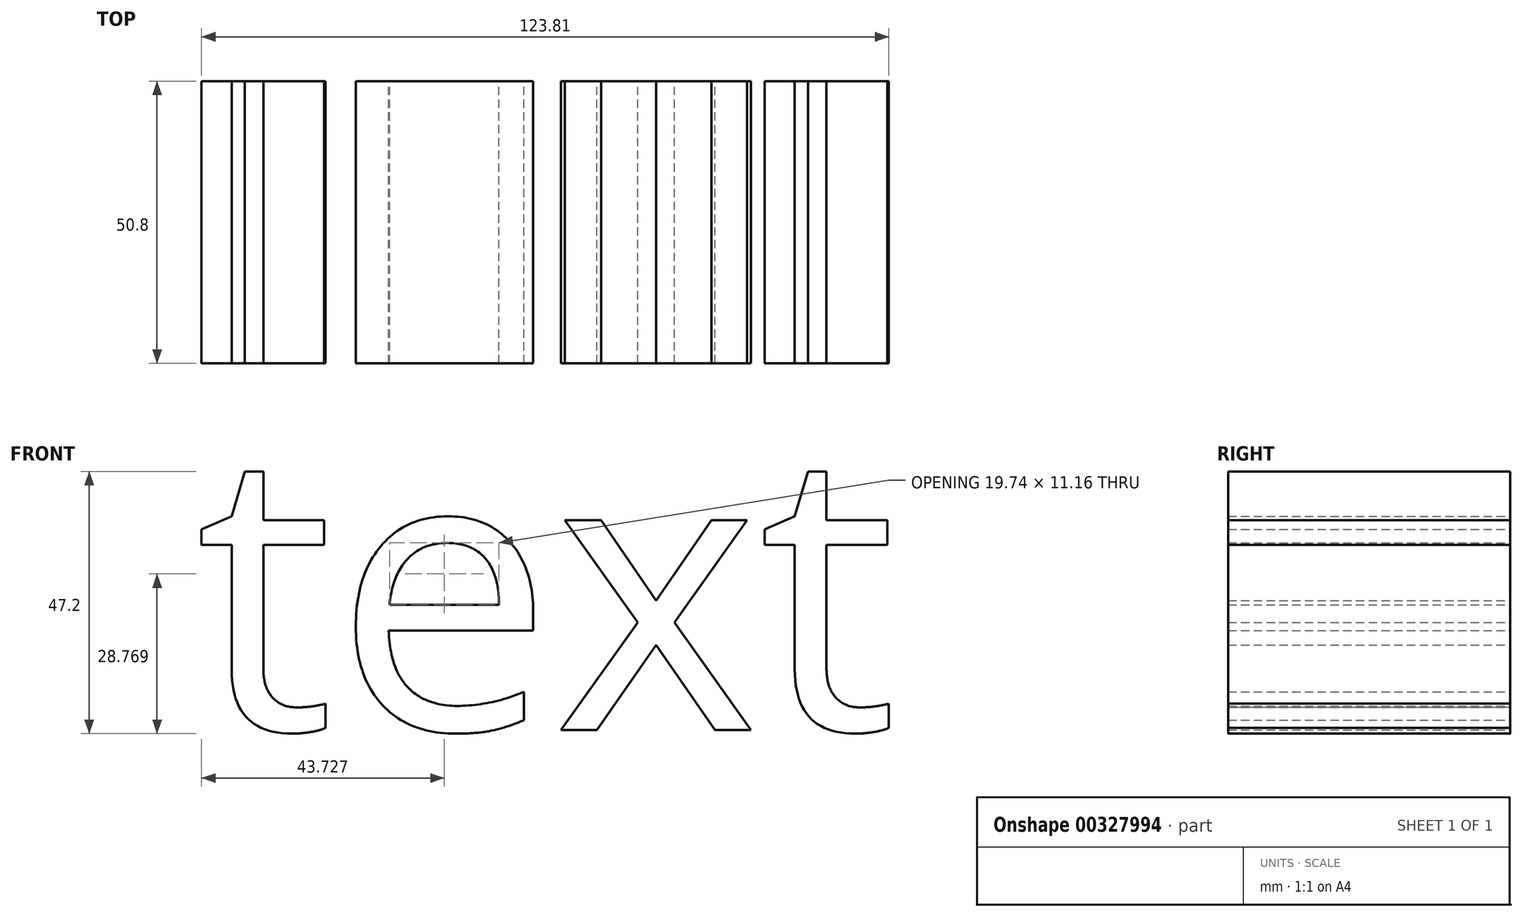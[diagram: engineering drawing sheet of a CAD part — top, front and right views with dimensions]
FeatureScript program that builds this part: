
annotation { "Feature Type Name" : "Feature", "Feature Type Description" : "" }
export const myFeature = defineFeature(function(context is Context, id is Id, definition is map)
    precondition{}
    {
        {
            var Q0;
            Q0=qCreatedBy(makeId("Front.planeOp"),FACE);
            var sketch = newSketch(context, id + "F0", { "sketchPlane" : qUnion([Q0])});
            skText(sketch, "E0", { "text": "text\n", "fontName": "OpenSans-Regular.ttf"});
            const initialGuessF0  = {"E0": [-0.03155, -0.02577, 1, 0, 0.0508]};
            skSetInitialGuess(sketch, initialGuessF0);
            skSolve(sketch);
        }
        {
            var Q0;
            Q0 = qSketchRegion(id + "F0", true);
            extrude(context, id + "F1", {"entities" : qUnion([Q0]), "depth" : 50.8 * mm});
        }
    });
